# Revit family: Boiler-Commercial_Remeha_P520
name_source: partatom
category: Mechanical Equipment
revit_build: Autodesk Revit MEP 2012 (Build: 20110309_2315(x64)
units: mm (PartAtom-declared; Revit-internal decimal feet)

## types (7) — shared parameters
Assembly Code = D3020100
Black = Black
Blue = Blue
Boiler Height incl top control panel - mm = 1760 mm  [stored 5.77428 ft]
Boiler Width - mm = 1172 mm
Clearance Box = Glass
Clearance box required = Yes
DarkGrey = DarkGrey
Description = P Series Cast Iron Boilers
Drain Outlet 3/4"  - 22mm = 22
Flue Gas temperature = < 190
Front Clearance Minimum = 1500 mm  [stored 4.92126 ft]
Front Clearance minimum  Note = Adapt this dimension on the basis of the dimensions of the burner.
Fuse Rating to control panel = 10 Amp
Green = Green
Grey = Grey
High Limit Thermostat deg C = 110
Host Condition = Floor Standing
Installation URL = http://www.remeha.co.uk
Light Grey = Light Grey
Manufacturer = Remeha Commercial
Manufacturer Fax = 0118 978 6977
Maximum operating pressure -  Bar = 6
Plumbing = Metal
Product Page URL = http://www.remeha.co.uk
Red = Red
Sales Brochure = http://remeha.co.uk
Side Clearance Mininum = 500 mm  [stored 1.64042 ft]
Side Clearance door opening side = 1200 mm
Side Clearance door opening side Note = Adapt this dimension on the basis of the dimensions of the burner.
Standard Operating Temperatures deg C = 30 - 90
Subcategory = Cast Iron Boilers
Top Clearance above case minimum = 850 mm  [stored 2.78871 ft]
URL = http://www.remeha.co.uk
Voltage to control panel = 230-1-50

## per-type parameters (varying)
| type | Boiler Length - Excluding Burner - mm | Flow Connection | Flow Connection Diameter | Flow Connection Radius | Flue Connection - mm | Hydraulic resistance at 10 dT - mbar | Hydraulic resistance at 20dT -  mbar | Mass flue gas flow  Gas Kg/h | Mass flue gas flow Fuel oil Kg/hr | Nominal flow rate at 20dT | Number of sections | Rated output kW | Rear Clearance | Return Connection | Return Connection Diameter | Return Connection Radius | Water content litres |
| P520 - 25 | 3355 mm | 159 mm  [stored 0.521654 ft] | 159 mm  [stored 0.521654 ft] | 80 mm | ** | 78.4 | 19.6 | 2070 | 1970
1970 | 17.32 | 25 | 1450 | 1266 mm  [stored 4.15354 ft] | 159 mm  [stored 0.521654 ft] | 159 mm  [stored 0.521654 ft] | 80 mm | 1095 |
| P520 - 23 | 3155 mm  [stored 10.351 ft] | 159 mm  [stored 0.521654 ft] | 159 mm  [stored 0.521654 ft] | 80 mm | ** | 64.8 | 16.2 | 1910 | 1820 | 15.93 | 23 | 1334 | 1266 mm  [stored 4.15354 ft] | 159 mm  [stored 0.521654 ft] | 159 mm  [stored 0.521654 ft] | 80 mm | 1019 |
| P520 - 21 | 2955 mm  [stored 9.69488 ft] | 159 mm  [stored 0.521654 ft] | 159 mm  [stored 0.521654 ft] | 80 mm | ** | 53.6 | 13.4 | 1750 | 1670 | 14.55 | 21 | 1218 | 936 mm  [stored 3.07087 ft] | 159 mm  [stored 0.521654 ft] | 159 mm  [stored 0.521654 ft] | 80 mm | 943 |
| P520 - 19 | 2645 mm  [stored 8.67782 ft] | 159 mm  [stored 0.521654 ft] | 159 mm  [stored 0.521654 ft] | 80 mm | 400 | 41.4 | 10.4 | 1590 | 1520 | 13.16 | 19 | 1102 | 656 mm  [stored 2.15223 ft] | 159 mm  [stored 0.521654 ft] | 159 mm  [stored 0.521654 ft] | 80 mm | 845 |
| P520 - 17 | 2445 mm  [stored 8.02165 ft] | 140 mm | 140 mm | 70 mm | 400 | 30.2 | 7.6 | 1440 | 1370 | 11.78 | 17 | 986 | 656 mm  [stored 2.15223 ft] | 140 mm | 140 mm | 70 mm | 769 |
| P520 - 13 | 1955 mm  [stored 6.41404 ft] | 140 mm | 140 mm | 70 mm | 350 | 57.6 | 14.4 | 1120 | 1070 | 9.01 | 13 | 754 | 300 mm | 140 mm | 140 mm | 70 mm | 617 |
| P520 - 15 | 2445 mm  [stored 8.02165 ft] | 140 mm | 140 mm | 70 mm | 400 | 77.6 | 19.4 | 1280 | 1220 | 10.39 | 15 | 870 | 436 mm  [stored 1.43045 ft] | 140 mm | 140 mm | 70 mm | 693 |

note: column(s) folded — value = type name in every type: Model

note: [stored X ft] marks values corroborated as IEEE doubles in the binary element streams (Revit-internal decimal feet)

## geometry (parser evidence)
native form markers: Sweep x1
no freeform markers — native parametric forms only
